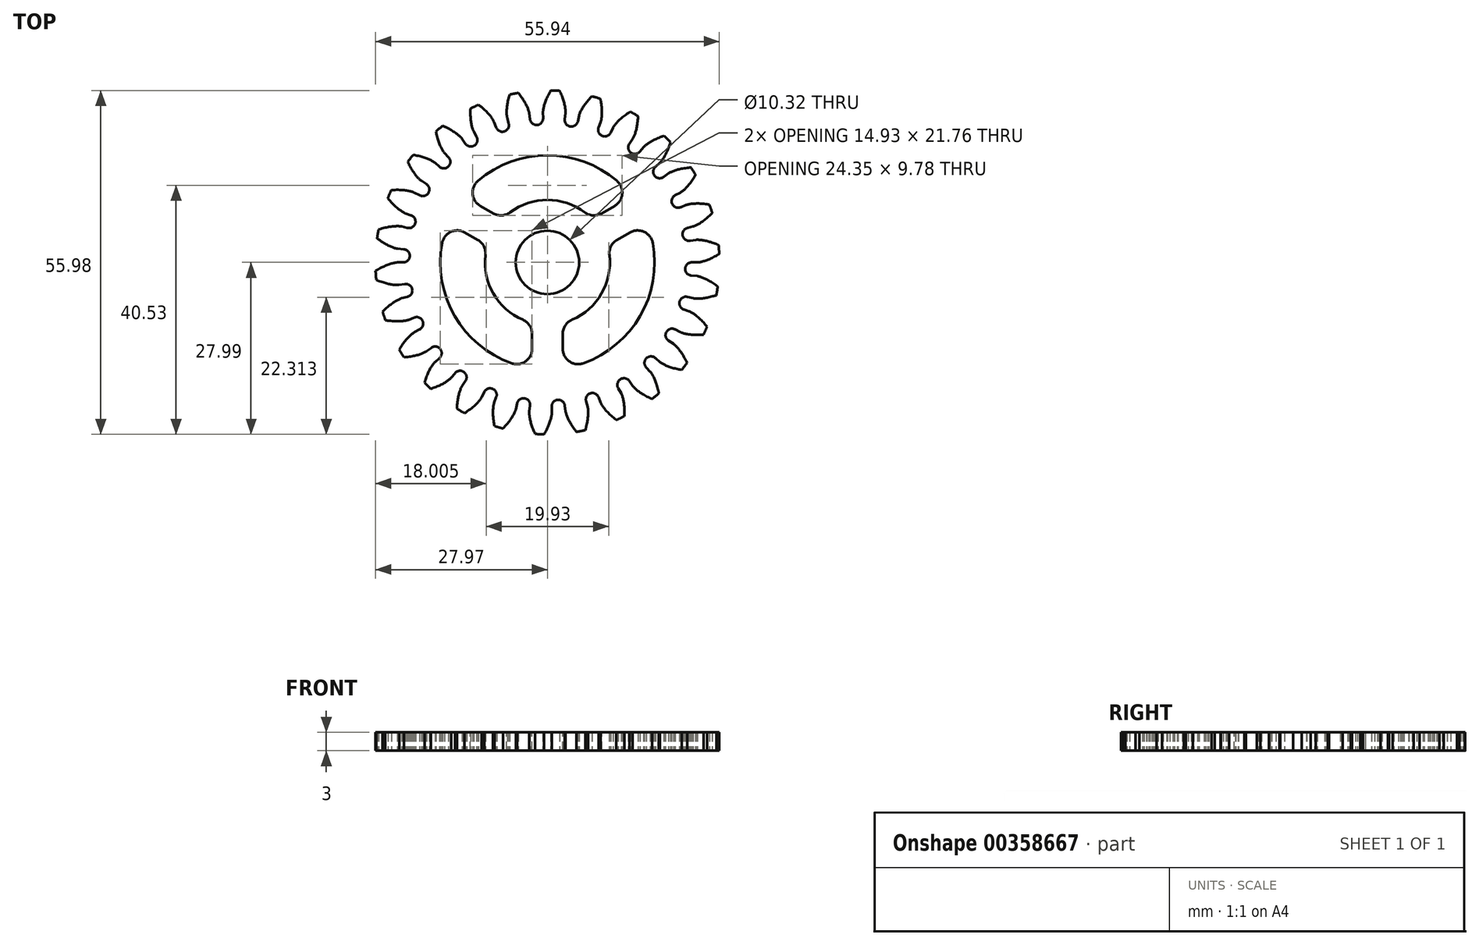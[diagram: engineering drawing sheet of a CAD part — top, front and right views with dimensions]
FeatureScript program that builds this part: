
annotation { "Feature Type Name" : "Feature", "Feature Type Description" : "" }
export const myFeature = defineFeature(function(context is Context, id is Id, definition is map)
    precondition{}
    {
        {
            assignVariable(context, id + "F0", {"name" : "T", "anyValue" : 26});
        }
        {
            assignVariable(context, id + "F1", {"name" : "SP", "anyValue" : 3});
        }
        {
            assignVariable(context, id + "F2", {"name" : "SF", "anyValue" : 2.5});
        }
        {
            var Q0;
            Q0=qCreatedBy(makeId("Top.planeOp"),FACE);
            var sketch = newSketch(context, id + "F3", { "sketchPlane" : qUnion([Q0])});
            skCircle(sketch, "E0", {"center": v(0, 0) * mm, "radius": 28 * mm});
            skCircle(sketch, "E1", {"center": v(0, 0) * mm, "radius": 26 * mm, "construction": true});
            skCircle(sketch, "E2", {"center": v(0, 0) * mm, "radius": 24.43 * mm, "construction": true});
            skCircle(sketch, "E3", {"center": v(0, 0) * mm, "radius": 23.5 * mm});
            skLineSegment(sketch, "E4", {"start": v(0, 0) * mm, "end": v(24.43, 0) * mm});
            skFitSpline(sketch, "E5", {"points": [v(24.43, 0) * mm, v(24.47, 0) * mm, v(24.6, 0.01) * mm, v(24.8, 0.04) * mm, v(25.1, 0.1) * mm, v(25.46, 0.2) * mm, v(25.9, 0.35) * mm, v(26.41, 0.56) * mm, v(26.99, 0.83) * mm, v(27.62, 1.17) * mm, v(28.3, 1.6) * mm], "startDerivative": vector(3.78, 0.15) * mm, "endDerivative": vector(13.99, 8.75) * mm});
            skLineSegment(sketch, "E6", {"start": v(0, 0) * mm, "end": v(27.97, -1.27) * mm, "construction": true});
            skLineSegment(sketch, "E7", {"start": v(0, 0) * mm, "end": v(26, 0.39) * mm, "construction": true});
            skFitSpline(sketch, "E8.MirrorCS", {"points": [v(24.33, -2.22) * mm, v(24.37, -2.23) * mm, v(24.5, -2.25) * mm, v(24.7, -2.3) * mm, v(24.98, -2.39) * mm, v(25.34, -2.52) * mm, v(25.77, -2.7) * mm, v(26.25, -2.96) * mm, v(26.8, -3.28) * mm, v(27.4, -3.68) * mm, v(28.03, -4.16) * mm], "startDerivative": vector(3.75, -0.5) * mm, "endDerivative": vector(13.13, -9.98) * mm});
            skLineSegment(sketch, "E9", {"start": v(0, 0) * mm, "end": v(24.33, -2.22) * mm});
            skSolve(sketch);
        }
        {
            var Q0;
            Q0=qCreatedBy(makeId("Top.planeOp"),FACE);
            var sketch = newSketch(context, id + "F4", { "sketchPlane" : qUnion([Q0])});
            skCircle(sketch, "E10", {"center": v(0, 0) * mm, "radius": 28 * mm});
            skSolve(sketch);
        }
        {
            var Q0;
            {var subQ0=sQuery(id+"F3.wireOp",EDGE,"E5");var subQ7=sQuery(id+"F3.wireOp",EDGE,"E0");var subQ8=makeQuery(id+"F3.imprint","INTERSECT",VERTEX,{"derivedFrom":[subQ7,subQ0]});Q0=makeQuery(id+"F3.imprint","IMPRINT",FACE,{"disambiguationData":[TD([[makeQuery(id+"F3.imprint","IMPRINT",EDGE,{"disambiguationData":[TD([[subQ8,1.0]])],"derivedFrom":subQ7}),1.0]])]});}
            extrude(context, id + "F5", {"entities" : qUnion([Q0]), "depth" : 6 * mm});
        }
        {
            var Q0;
            Q0=makeQuery(id+"F5.opExtrude","CAP_FACE",FACE,{"disambiguationData":[OSD([sQuery(id+"F3.wireOp",EDGE,"E0"),sQuery(id+"F3.wireOp",EDGE,"E3"),sQuery(id+"F3.wireOp",EDGE,"E4"),sQuery(id+"F3.wireOp",EDGE,"E5"),sQuery(id+"F3.wireOp",EDGE,"E8.MirrorCS"),sQuery(id+"F3.wireOp",EDGE,"E9")])],"isStart":true});
            var sketch = newSketch(context, id + "F6", { "sketchPlane" : qUnion([Q0])});
            skCircle(sketch, "E11", {"center": v(23.48, 1.07) * mm, "radius": 1.07 * mm});
            skSolve(sketch);
        }
        {
            var Q0;
            {var subQ1=makeQuery(id+"F5.opExtrude","CAP_EDGE",EDGE,{"disambiguationData":[OSD([sQuery(id+"F3.wireOp",EDGE,"E3")])],"isStart":true});Q0=makeQuery(id+"F6.imprint","IMPRINT",FACE,{"disambiguationData":[TD([[makeQuery(id+"F6.imprint","IMPRINT",EDGE,{"derivedFrom":subQ1}),-1.0]])]});}
            extrude(context, id + "F7", {"entities" : qUnion([Q0]), "operationType" : NewBodyOperationType.ADD, "oppositeDirection" : true, "depth" : 6 * mm});
        }
        {
            var Q0;
            Q0=makeQuery(id+"F4.imprint","IMPRINT",FACE,{"disambiguationData":[TD([[makeQuery(id+"F4.imprint","IMPRINT",EDGE,{"derivedFrom":sQuery(id+"F4.wireOp",EDGE,"E10")}),1.0]])]});
            extrude(context, id + "F8", {"entities" : qUnion([Q0]), "depth" : 3 * mm, "offsetDistance" : 25 * mm});
        }
        {
            var Q0;
            Q0=makeQuery(id+"F5.opExtrude","SWEPT_BODY",BODY,{"disambiguationData":[OSD([sQuery(id+"F3.wireOp",EDGE,"E0"),sQuery(id+"F3.wireOp",EDGE,"E3"),sQuery(id+"F3.wireOp",EDGE,"E4"),sQuery(id+"F3.wireOp",EDGE,"E5"),sQuery(id+"F3.wireOp",EDGE,"E8.MirrorCS"),sQuery(id+"F3.wireOp",EDGE,"E9")])]});
            var Q1;
            Q1=makeQuery(id+"F8.opExtrude","CAP_EDGE",EDGE,{"disambiguationData":[OSD([sQuery(id+"F4.wireOp",EDGE,"E10")])],"isStart":false});
            circularPattern(context, id + "F9", {"entities" : qUnion([Q0]), "axis" : qUnion([Q1]), "angle" : 360 * degree, "instanceCount" : getVariable(context, 'T'), "equalSpace" : true});
        }
        {
            var Q0;
            Q0=makeQuery(id+"F9.opPattern","COPY",BODY,{"derivedFrom":makeQuery(id+"F5.opExtrude","SWEPT_BODY",BODY,{"disambiguationData":[OSD([sQuery(id+"F3.wireOp",EDGE,"E0"),sQuery(id+"F3.wireOp",EDGE,"E3"),sQuery(id+"F3.wireOp",EDGE,"E4"),sQuery(id+"F3.wireOp",EDGE,"E5"),sQuery(id+"F3.wireOp",EDGE,"E8.MirrorCS"),sQuery(id+"F3.wireOp",EDGE,"E9")])]}),"instanceName":"5"});
            var Q1;
            Q1=makeQuery(id+"F9.opPattern","COPY",BODY,{"derivedFrom":makeQuery(id+"F5.opExtrude","SWEPT_BODY",BODY,{"disambiguationData":[OSD([sQuery(id+"F3.wireOp",EDGE,"E0"),sQuery(id+"F3.wireOp",EDGE,"E3"),sQuery(id+"F3.wireOp",EDGE,"E4"),sQuery(id+"F3.wireOp",EDGE,"E5"),sQuery(id+"F3.wireOp",EDGE,"E8.MirrorCS"),sQuery(id+"F3.wireOp",EDGE,"E9")])]}),"instanceName":"6"});
            var Q2;
            Q2=makeQuery(id+"F9.opPattern","COPY",BODY,{"derivedFrom":makeQuery(id+"F5.opExtrude","SWEPT_BODY",BODY,{"disambiguationData":[OSD([sQuery(id+"F3.wireOp",EDGE,"E0"),sQuery(id+"F3.wireOp",EDGE,"E3"),sQuery(id+"F3.wireOp",EDGE,"E4"),sQuery(id+"F3.wireOp",EDGE,"E5"),sQuery(id+"F3.wireOp",EDGE,"E8.MirrorCS"),sQuery(id+"F3.wireOp",EDGE,"E9")])]}),"instanceName":"7"});
            var Q3;
            Q3=makeQuery(id+"F9.opPattern","COPY",BODY,{"derivedFrom":makeQuery(id+"F5.opExtrude","SWEPT_BODY",BODY,{"disambiguationData":[OSD([sQuery(id+"F3.wireOp",EDGE,"E0"),sQuery(id+"F3.wireOp",EDGE,"E3"),sQuery(id+"F3.wireOp",EDGE,"E4"),sQuery(id+"F3.wireOp",EDGE,"E5"),sQuery(id+"F3.wireOp",EDGE,"E8.MirrorCS"),sQuery(id+"F3.wireOp",EDGE,"E9")])]}),"instanceName":"8"});
            var Q4;
            Q4=makeQuery(id+"F9.opPattern","COPY",BODY,{"derivedFrom":makeQuery(id+"F5.opExtrude","SWEPT_BODY",BODY,{"disambiguationData":[OSD([sQuery(id+"F3.wireOp",EDGE,"E0"),sQuery(id+"F3.wireOp",EDGE,"E3"),sQuery(id+"F3.wireOp",EDGE,"E4"),sQuery(id+"F3.wireOp",EDGE,"E5"),sQuery(id+"F3.wireOp",EDGE,"E8.MirrorCS"),sQuery(id+"F3.wireOp",EDGE,"E9")])]}),"instanceName":"9"});
            var Q5;
            Q5=makeQuery(id+"F9.opPattern","COPY",BODY,{"derivedFrom":makeQuery(id+"F5.opExtrude","SWEPT_BODY",BODY,{"disambiguationData":[OSD([sQuery(id+"F3.wireOp",EDGE,"E0"),sQuery(id+"F3.wireOp",EDGE,"E3"),sQuery(id+"F3.wireOp",EDGE,"E4"),sQuery(id+"F3.wireOp",EDGE,"E5"),sQuery(id+"F3.wireOp",EDGE,"E8.MirrorCS"),sQuery(id+"F3.wireOp",EDGE,"E9")])]}),"instanceName":"10"});
            var Q6;
            Q6=makeQuery(id+"F9.opPattern","COPY",BODY,{"derivedFrom":makeQuery(id+"F5.opExtrude","SWEPT_BODY",BODY,{"disambiguationData":[OSD([sQuery(id+"F3.wireOp",EDGE,"E0"),sQuery(id+"F3.wireOp",EDGE,"E3"),sQuery(id+"F3.wireOp",EDGE,"E4"),sQuery(id+"F3.wireOp",EDGE,"E5"),sQuery(id+"F3.wireOp",EDGE,"E8.MirrorCS"),sQuery(id+"F3.wireOp",EDGE,"E9")])]}),"instanceName":"11"});
            var Q7;
            Q7=makeQuery(id+"F9.opPattern","COPY",BODY,{"derivedFrom":makeQuery(id+"F5.opExtrude","SWEPT_BODY",BODY,{"disambiguationData":[OSD([sQuery(id+"F3.wireOp",EDGE,"E0"),sQuery(id+"F3.wireOp",EDGE,"E3"),sQuery(id+"F3.wireOp",EDGE,"E4"),sQuery(id+"F3.wireOp",EDGE,"E5"),sQuery(id+"F3.wireOp",EDGE,"E8.MirrorCS"),sQuery(id+"F3.wireOp",EDGE,"E9")])]}),"instanceName":"12"});
            var Q8;
            Q8=makeQuery(id+"F9.opPattern","COPY",BODY,{"derivedFrom":makeQuery(id+"F5.opExtrude","SWEPT_BODY",BODY,{"disambiguationData":[OSD([sQuery(id+"F3.wireOp",EDGE,"E0"),sQuery(id+"F3.wireOp",EDGE,"E3"),sQuery(id+"F3.wireOp",EDGE,"E4"),sQuery(id+"F3.wireOp",EDGE,"E5"),sQuery(id+"F3.wireOp",EDGE,"E8.MirrorCS"),sQuery(id+"F3.wireOp",EDGE,"E9")])]}),"instanceName":"13"});
            var Q9;
            Q9=makeQuery(id+"F9.opPattern","COPY",BODY,{"derivedFrom":makeQuery(id+"F5.opExtrude","SWEPT_BODY",BODY,{"disambiguationData":[OSD([sQuery(id+"F3.wireOp",EDGE,"E0"),sQuery(id+"F3.wireOp",EDGE,"E3"),sQuery(id+"F3.wireOp",EDGE,"E4"),sQuery(id+"F3.wireOp",EDGE,"E5"),sQuery(id+"F3.wireOp",EDGE,"E8.MirrorCS"),sQuery(id+"F3.wireOp",EDGE,"E9")])]}),"instanceName":"14"});
            var Q10;
            Q10=makeQuery(id+"F9.opPattern","COPY",BODY,{"derivedFrom":makeQuery(id+"F5.opExtrude","SWEPT_BODY",BODY,{"disambiguationData":[OSD([sQuery(id+"F3.wireOp",EDGE,"E0"),sQuery(id+"F3.wireOp",EDGE,"E3"),sQuery(id+"F3.wireOp",EDGE,"E4"),sQuery(id+"F3.wireOp",EDGE,"E5"),sQuery(id+"F3.wireOp",EDGE,"E8.MirrorCS"),sQuery(id+"F3.wireOp",EDGE,"E9")])]}),"instanceName":"15"});
            var Q11;
            Q11=makeQuery(id+"F9.opPattern","COPY",BODY,{"derivedFrom":makeQuery(id+"F5.opExtrude","SWEPT_BODY",BODY,{"disambiguationData":[OSD([sQuery(id+"F3.wireOp",EDGE,"E0"),sQuery(id+"F3.wireOp",EDGE,"E3"),sQuery(id+"F3.wireOp",EDGE,"E4"),sQuery(id+"F3.wireOp",EDGE,"E5"),sQuery(id+"F3.wireOp",EDGE,"E8.MirrorCS"),sQuery(id+"F3.wireOp",EDGE,"E9")])]}),"instanceName":"16"});
            var Q12;
            Q12=makeQuery(id+"F9.opPattern","COPY",BODY,{"derivedFrom":makeQuery(id+"F5.opExtrude","SWEPT_BODY",BODY,{"disambiguationData":[OSD([sQuery(id+"F3.wireOp",EDGE,"E0"),sQuery(id+"F3.wireOp",EDGE,"E3"),sQuery(id+"F3.wireOp",EDGE,"E4"),sQuery(id+"F3.wireOp",EDGE,"E5"),sQuery(id+"F3.wireOp",EDGE,"E8.MirrorCS"),sQuery(id+"F3.wireOp",EDGE,"E9")])]}),"instanceName":"17"});
            var Q13;
            Q13=makeQuery(id+"F9.opPattern","COPY",BODY,{"derivedFrom":makeQuery(id+"F5.opExtrude","SWEPT_BODY",BODY,{"disambiguationData":[OSD([sQuery(id+"F3.wireOp",EDGE,"E0"),sQuery(id+"F3.wireOp",EDGE,"E3"),sQuery(id+"F3.wireOp",EDGE,"E4"),sQuery(id+"F3.wireOp",EDGE,"E5"),sQuery(id+"F3.wireOp",EDGE,"E8.MirrorCS"),sQuery(id+"F3.wireOp",EDGE,"E9")])]}),"instanceName":"18"});
            var Q14;
            Q14=makeQuery(id+"F9.opPattern","COPY",BODY,{"derivedFrom":makeQuery(id+"F5.opExtrude","SWEPT_BODY",BODY,{"disambiguationData":[OSD([sQuery(id+"F3.wireOp",EDGE,"E0"),sQuery(id+"F3.wireOp",EDGE,"E3"),sQuery(id+"F3.wireOp",EDGE,"E4"),sQuery(id+"F3.wireOp",EDGE,"E5"),sQuery(id+"F3.wireOp",EDGE,"E8.MirrorCS"),sQuery(id+"F3.wireOp",EDGE,"E9")])]}),"instanceName":"19"});
            var Q15;
            Q15=makeQuery(id+"F9.opPattern","COPY",BODY,{"derivedFrom":makeQuery(id+"F5.opExtrude","SWEPT_BODY",BODY,{"disambiguationData":[OSD([sQuery(id+"F3.wireOp",EDGE,"E0"),sQuery(id+"F3.wireOp",EDGE,"E3"),sQuery(id+"F3.wireOp",EDGE,"E4"),sQuery(id+"F3.wireOp",EDGE,"E5"),sQuery(id+"F3.wireOp",EDGE,"E8.MirrorCS"),sQuery(id+"F3.wireOp",EDGE,"E9")])]}),"instanceName":"20"});
            var Q16;
            Q16=makeQuery(id+"F9.opPattern","COPY",BODY,{"derivedFrom":makeQuery(id+"F5.opExtrude","SWEPT_BODY",BODY,{"disambiguationData":[OSD([sQuery(id+"F3.wireOp",EDGE,"E0"),sQuery(id+"F3.wireOp",EDGE,"E3"),sQuery(id+"F3.wireOp",EDGE,"E4"),sQuery(id+"F3.wireOp",EDGE,"E5"),sQuery(id+"F3.wireOp",EDGE,"E8.MirrorCS"),sQuery(id+"F3.wireOp",EDGE,"E9")])]}),"instanceName":"21"});
            var Q17;
            Q17=makeQuery(id+"F9.opPattern","COPY",BODY,{"derivedFrom":makeQuery(id+"F5.opExtrude","SWEPT_BODY",BODY,{"disambiguationData":[OSD([sQuery(id+"F3.wireOp",EDGE,"E0"),sQuery(id+"F3.wireOp",EDGE,"E3"),sQuery(id+"F3.wireOp",EDGE,"E4"),sQuery(id+"F3.wireOp",EDGE,"E5"),sQuery(id+"F3.wireOp",EDGE,"E8.MirrorCS"),sQuery(id+"F3.wireOp",EDGE,"E9")])]}),"instanceName":"22"});
            var Q18;
            Q18=makeQuery(id+"F9.opPattern","COPY",BODY,{"derivedFrom":makeQuery(id+"F5.opExtrude","SWEPT_BODY",BODY,{"disambiguationData":[OSD([sQuery(id+"F3.wireOp",EDGE,"E0"),sQuery(id+"F3.wireOp",EDGE,"E3"),sQuery(id+"F3.wireOp",EDGE,"E4"),sQuery(id+"F3.wireOp",EDGE,"E5"),sQuery(id+"F3.wireOp",EDGE,"E8.MirrorCS"),sQuery(id+"F3.wireOp",EDGE,"E9")])]}),"instanceName":"23"});
            var Q19;
            Q19=makeQuery(id+"F9.opPattern","COPY",BODY,{"derivedFrom":makeQuery(id+"F5.opExtrude","SWEPT_BODY",BODY,{"disambiguationData":[OSD([sQuery(id+"F3.wireOp",EDGE,"E0"),sQuery(id+"F3.wireOp",EDGE,"E3"),sQuery(id+"F3.wireOp",EDGE,"E4"),sQuery(id+"F3.wireOp",EDGE,"E5"),sQuery(id+"F3.wireOp",EDGE,"E8.MirrorCS"),sQuery(id+"F3.wireOp",EDGE,"E9")])]}),"instanceName":"24"});
            var Q20;
            Q20=makeQuery(id+"F9.opPattern","COPY",BODY,{"derivedFrom":makeQuery(id+"F5.opExtrude","SWEPT_BODY",BODY,{"disambiguationData":[OSD([sQuery(id+"F3.wireOp",EDGE,"E0"),sQuery(id+"F3.wireOp",EDGE,"E3"),sQuery(id+"F3.wireOp",EDGE,"E4"),sQuery(id+"F3.wireOp",EDGE,"E5"),sQuery(id+"F3.wireOp",EDGE,"E8.MirrorCS"),sQuery(id+"F3.wireOp",EDGE,"E9")])]}),"instanceName":"25"});
            var Q21;
            Q21=makeQuery(id+"F9.opPattern","COPY",BODY,{"derivedFrom":makeQuery(id+"F5.opExtrude","SWEPT_BODY",BODY,{"disambiguationData":[OSD([sQuery(id+"F3.wireOp",EDGE,"E0"),sQuery(id+"F3.wireOp",EDGE,"E3"),sQuery(id+"F3.wireOp",EDGE,"E4"),sQuery(id+"F3.wireOp",EDGE,"E5"),sQuery(id+"F3.wireOp",EDGE,"E8.MirrorCS"),sQuery(id+"F3.wireOp",EDGE,"E9")])]}),"instanceName":"26"});
            var Q22;
            Q22=makeQuery(id+"F9.opPattern","COPY",BODY,{"derivedFrom":makeQuery(id+"F5.opExtrude","SWEPT_BODY",BODY,{"disambiguationData":[OSD([sQuery(id+"F3.wireOp",EDGE,"E0"),sQuery(id+"F3.wireOp",EDGE,"E3"),sQuery(id+"F3.wireOp",EDGE,"E4"),sQuery(id+"F3.wireOp",EDGE,"E5"),sQuery(id+"F3.wireOp",EDGE,"E8.MirrorCS"),sQuery(id+"F3.wireOp",EDGE,"E9")])]}),"instanceName":"27"});
            var Q23;
            Q23=makeQuery(id+"F9.opPattern","COPY",BODY,{"derivedFrom":makeQuery(id+"F5.opExtrude","SWEPT_BODY",BODY,{"disambiguationData":[OSD([sQuery(id+"F3.wireOp",EDGE,"E0"),sQuery(id+"F3.wireOp",EDGE,"E3"),sQuery(id+"F3.wireOp",EDGE,"E4"),sQuery(id+"F3.wireOp",EDGE,"E5"),sQuery(id+"F3.wireOp",EDGE,"E8.MirrorCS"),sQuery(id+"F3.wireOp",EDGE,"E9")])]}),"instanceName":"28"});
            var Q24;
            Q24=makeQuery(id+"F9.opPattern","COPY",BODY,{"derivedFrom":makeQuery(id+"F5.opExtrude","SWEPT_BODY",BODY,{"disambiguationData":[OSD([sQuery(id+"F3.wireOp",EDGE,"E0"),sQuery(id+"F3.wireOp",EDGE,"E3"),sQuery(id+"F3.wireOp",EDGE,"E4"),sQuery(id+"F3.wireOp",EDGE,"E5"),sQuery(id+"F3.wireOp",EDGE,"E8.MirrorCS"),sQuery(id+"F3.wireOp",EDGE,"E9")])]}),"instanceName":"29"});
            var Q25;
            Q25=makeQuery(id+"F5.opExtrude","SWEPT_BODY",BODY,{"disambiguationData":[OSD([sQuery(id+"F3.wireOp",EDGE,"E0"),sQuery(id+"F3.wireOp",EDGE,"E3"),sQuery(id+"F3.wireOp",EDGE,"E4"),sQuery(id+"F3.wireOp",EDGE,"E5"),sQuery(id+"F3.wireOp",EDGE,"E8.MirrorCS"),sQuery(id+"F3.wireOp",EDGE,"E9")])]});
            var Q26;
            Q26=makeQuery(id+"F9.opPattern","COPY",BODY,{"derivedFrom":makeQuery(id+"F5.opExtrude","SWEPT_BODY",BODY,{"disambiguationData":[OSD([sQuery(id+"F3.wireOp",EDGE,"E0"),sQuery(id+"F3.wireOp",EDGE,"E3"),sQuery(id+"F3.wireOp",EDGE,"E4"),sQuery(id+"F3.wireOp",EDGE,"E5"),sQuery(id+"F3.wireOp",EDGE,"E8.MirrorCS"),sQuery(id+"F3.wireOp",EDGE,"E9")])]}),"instanceName":"1"});
            var Q27;
            Q27=makeQuery(id+"F9.opPattern","COPY",BODY,{"derivedFrom":makeQuery(id+"F5.opExtrude","SWEPT_BODY",BODY,{"disambiguationData":[OSD([sQuery(id+"F3.wireOp",EDGE,"E0"),sQuery(id+"F3.wireOp",EDGE,"E3"),sQuery(id+"F3.wireOp",EDGE,"E4"),sQuery(id+"F3.wireOp",EDGE,"E5"),sQuery(id+"F3.wireOp",EDGE,"E8.MirrorCS"),sQuery(id+"F3.wireOp",EDGE,"E9")])]}),"instanceName":"2"});
            var Q28;
            Q28=makeQuery(id+"F9.opPattern","COPY",BODY,{"derivedFrom":makeQuery(id+"F5.opExtrude","SWEPT_BODY",BODY,{"disambiguationData":[OSD([sQuery(id+"F3.wireOp",EDGE,"E0"),sQuery(id+"F3.wireOp",EDGE,"E3"),sQuery(id+"F3.wireOp",EDGE,"E4"),sQuery(id+"F3.wireOp",EDGE,"E5"),sQuery(id+"F3.wireOp",EDGE,"E8.MirrorCS"),sQuery(id+"F3.wireOp",EDGE,"E9")])]}),"instanceName":"3"});
            var Q29;
            Q29=makeQuery(id+"F9.opPattern","COPY",BODY,{"derivedFrom":makeQuery(id+"F5.opExtrude","SWEPT_BODY",BODY,{"disambiguationData":[OSD([sQuery(id+"F3.wireOp",EDGE,"E0"),sQuery(id+"F3.wireOp",EDGE,"E3"),sQuery(id+"F3.wireOp",EDGE,"E4"),sQuery(id+"F3.wireOp",EDGE,"E5"),sQuery(id+"F3.wireOp",EDGE,"E8.MirrorCS"),sQuery(id+"F3.wireOp",EDGE,"E9")])]}),"instanceName":"4"});
            var Q30;
            Q30=makeQuery(id+"F9.opPattern","COPY",BODY,{"derivedFrom":makeQuery(id+"F5.opExtrude","SWEPT_BODY",BODY,{"disambiguationData":[OSD([sQuery(id+"F3.wireOp",EDGE,"E0"),sQuery(id+"F3.wireOp",EDGE,"E3"),sQuery(id+"F3.wireOp",EDGE,"E5"),sQuery(id+"F3.wireOp",EDGE,"E8.MirrorCS")])]}),"instanceName":"30"});
            var Q31;
            Q31=makeQuery(id+"F9.opPattern","COPY",BODY,{"derivedFrom":makeQuery(id+"F5.opExtrude","SWEPT_BODY",BODY,{"disambiguationData":[OSD([sQuery(id+"F3.wireOp",EDGE,"E0"),sQuery(id+"F3.wireOp",EDGE,"E3"),sQuery(id+"F3.wireOp",EDGE,"E5"),sQuery(id+"F3.wireOp",EDGE,"E8.MirrorCS")])]}),"instanceName":"31"});
            var Q32;
            Q32=makeQuery(id+"F9.opPattern","COPY",BODY,{"derivedFrom":makeQuery(id+"F5.opExtrude","SWEPT_BODY",BODY,{"disambiguationData":[OSD([sQuery(id+"F3.wireOp",EDGE,"E0"),sQuery(id+"F3.wireOp",EDGE,"E3"),sQuery(id+"F3.wireOp",EDGE,"E5"),sQuery(id+"F3.wireOp",EDGE,"E8.MirrorCS")])]}),"instanceName":"32"});
            var Q33;
            Q33=makeQuery(id+"F9.opPattern","COPY",BODY,{"derivedFrom":makeQuery(id+"F5.opExtrude","SWEPT_BODY",BODY,{"disambiguationData":[OSD([sQuery(id+"F3.wireOp",EDGE,"E0"),sQuery(id+"F3.wireOp",EDGE,"E3"),sQuery(id+"F3.wireOp",EDGE,"E5"),sQuery(id+"F3.wireOp",EDGE,"E8.MirrorCS")])]}),"instanceName":"33"});
            var Q34;
            Q34=makeQuery(id+"F9.opPattern","COPY",BODY,{"derivedFrom":makeQuery(id+"F5.opExtrude","SWEPT_BODY",BODY,{"disambiguationData":[OSD([sQuery(id+"F3.wireOp",EDGE,"E0"),sQuery(id+"F3.wireOp",EDGE,"E3"),sQuery(id+"F3.wireOp",EDGE,"E5"),sQuery(id+"F3.wireOp",EDGE,"E8.MirrorCS")])]}),"instanceName":"34"});
            var Q35;
            Q35=makeQuery(id+"F9.opPattern","COPY",BODY,{"derivedFrom":makeQuery(id+"F5.opExtrude","SWEPT_BODY",BODY,{"disambiguationData":[OSD([sQuery(id+"F3.wireOp",EDGE,"E0"),sQuery(id+"F3.wireOp",EDGE,"E3"),sQuery(id+"F3.wireOp",EDGE,"E5"),sQuery(id+"F3.wireOp",EDGE,"E8.MirrorCS")])]}),"instanceName":"35"});
            var Q36;
            Q36=makeQuery(id+"F9.opPattern","COPY",BODY,{"derivedFrom":makeQuery(id+"F5.opExtrude","SWEPT_BODY",BODY,{"disambiguationData":[OSD([sQuery(id+"F3.wireOp",EDGE,"E0"),sQuery(id+"F3.wireOp",EDGE,"E3"),sQuery(id+"F3.wireOp",EDGE,"E5"),sQuery(id+"F3.wireOp",EDGE,"E8.MirrorCS")])]}),"instanceName":"36"});
            var Q37;
            Q37=makeQuery(id+"F9.opPattern","COPY",BODY,{"derivedFrom":makeQuery(id+"F5.opExtrude","SWEPT_BODY",BODY,{"disambiguationData":[OSD([sQuery(id+"F3.wireOp",EDGE,"E0"),sQuery(id+"F3.wireOp",EDGE,"E3"),sQuery(id+"F3.wireOp",EDGE,"E5"),sQuery(id+"F3.wireOp",EDGE,"E8.MirrorCS")])]}),"instanceName":"37"});
            var Q38;
            Q38=makeQuery(id+"F9.opPattern","COPY",BODY,{"derivedFrom":makeQuery(id+"F5.opExtrude","SWEPT_BODY",BODY,{"disambiguationData":[OSD([sQuery(id+"F3.wireOp",EDGE,"E0"),sQuery(id+"F3.wireOp",EDGE,"E3"),sQuery(id+"F3.wireOp",EDGE,"E5"),sQuery(id+"F3.wireOp",EDGE,"E8.MirrorCS")])]}),"instanceName":"38"});
            var Q39;
            Q39=makeQuery(id+"F9.opPattern","COPY",BODY,{"derivedFrom":makeQuery(id+"F5.opExtrude","SWEPT_BODY",BODY,{"disambiguationData":[OSD([sQuery(id+"F3.wireOp",EDGE,"E0"),sQuery(id+"F3.wireOp",EDGE,"E3"),sQuery(id+"F3.wireOp",EDGE,"E5"),sQuery(id+"F3.wireOp",EDGE,"E8.MirrorCS")])]}),"instanceName":"39"});
            var Q40;
            Q40=makeQuery(id+"F9.opPattern","COPY",BODY,{"derivedFrom":makeQuery(id+"F5.opExtrude","SWEPT_BODY",BODY,{"disambiguationData":[OSD([sQuery(id+"F3.wireOp",EDGE,"E0"),sQuery(id+"F3.wireOp",EDGE,"E3"),sQuery(id+"F3.wireOp",EDGE,"E5"),sQuery(id+"F3.wireOp",EDGE,"E8.MirrorCS")])]}),"instanceName":"40"});
            var Q41;
            Q41=makeQuery(id+"F9.opPattern","COPY",BODY,{"derivedFrom":makeQuery(id+"F5.opExtrude","SWEPT_BODY",BODY,{"disambiguationData":[OSD([sQuery(id+"F3.wireOp",EDGE,"E0"),sQuery(id+"F3.wireOp",EDGE,"E3"),sQuery(id+"F3.wireOp",EDGE,"E5"),sQuery(id+"F3.wireOp",EDGE,"E8.MirrorCS")])]}),"instanceName":"41"});
            var Q42;
            Q42=makeQuery(id+"F9.opPattern","COPY",BODY,{"derivedFrom":makeQuery(id+"F5.opExtrude","SWEPT_BODY",BODY,{"disambiguationData":[OSD([sQuery(id+"F3.wireOp",EDGE,"E0"),sQuery(id+"F3.wireOp",EDGE,"E3"),sQuery(id+"F3.wireOp",EDGE,"E5"),sQuery(id+"F3.wireOp",EDGE,"E8.MirrorCS")])]}),"instanceName":"42"});
            var Q43;
            Q43=makeQuery(id+"F9.opPattern","COPY",BODY,{"derivedFrom":makeQuery(id+"F5.opExtrude","SWEPT_BODY",BODY,{"disambiguationData":[OSD([sQuery(id+"F3.wireOp",EDGE,"E0"),sQuery(id+"F3.wireOp",EDGE,"E3"),sQuery(id+"F3.wireOp",EDGE,"E5"),sQuery(id+"F3.wireOp",EDGE,"E8.MirrorCS")])]}),"instanceName":"43"});
            var Q44;
            Q44=makeQuery(id+"F9.opPattern","COPY",BODY,{"derivedFrom":makeQuery(id+"F5.opExtrude","SWEPT_BODY",BODY,{"disambiguationData":[OSD([sQuery(id+"F3.wireOp",EDGE,"E0"),sQuery(id+"F3.wireOp",EDGE,"E3"),sQuery(id+"F3.wireOp",EDGE,"E5"),sQuery(id+"F3.wireOp",EDGE,"E8.MirrorCS")])]}),"instanceName":"44"});
            var Q45;
            Q45=makeQuery(id+"F9.opPattern","COPY",BODY,{"derivedFrom":makeQuery(id+"F5.opExtrude","SWEPT_BODY",BODY,{"disambiguationData":[OSD([sQuery(id+"F3.wireOp",EDGE,"E0"),sQuery(id+"F3.wireOp",EDGE,"E3"),sQuery(id+"F3.wireOp",EDGE,"E5"),sQuery(id+"F3.wireOp",EDGE,"E8.MirrorCS")])]}),"instanceName":"45"});
            var Q46;
            Q46=makeQuery(id+"F9.opPattern","COPY",BODY,{"derivedFrom":makeQuery(id+"F5.opExtrude","SWEPT_BODY",BODY,{"disambiguationData":[OSD([sQuery(id+"F3.wireOp",EDGE,"E0"),sQuery(id+"F3.wireOp",EDGE,"E3"),sQuery(id+"F3.wireOp",EDGE,"E5"),sQuery(id+"F3.wireOp",EDGE,"E8.MirrorCS")])]}),"instanceName":"46"});
            var Q47;
            Q47=makeQuery(id+"F9.opPattern","COPY",BODY,{"derivedFrom":makeQuery(id+"F5.opExtrude","SWEPT_BODY",BODY,{"disambiguationData":[OSD([sQuery(id+"F3.wireOp",EDGE,"E0"),sQuery(id+"F3.wireOp",EDGE,"E3"),sQuery(id+"F3.wireOp",EDGE,"E5"),sQuery(id+"F3.wireOp",EDGE,"E8.MirrorCS")])]}),"instanceName":"47"});
            var Q48;
            Q48=makeQuery(id+"F9.opPattern","COPY",BODY,{"derivedFrom":makeQuery(id+"F5.opExtrude","SWEPT_BODY",BODY,{"disambiguationData":[OSD([sQuery(id+"F3.wireOp",EDGE,"E0"),sQuery(id+"F3.wireOp",EDGE,"E3"),sQuery(id+"F3.wireOp",EDGE,"E5"),sQuery(id+"F3.wireOp",EDGE,"E8.MirrorCS")])]}),"instanceName":"48"});
            var Q49;
            Q49=makeQuery(id+"F9.opPattern","COPY",BODY,{"derivedFrom":makeQuery(id+"F5.opExtrude","SWEPT_BODY",BODY,{"disambiguationData":[OSD([sQuery(id+"F3.wireOp",EDGE,"E0"),sQuery(id+"F3.wireOp",EDGE,"E3"),sQuery(id+"F3.wireOp",EDGE,"E5"),sQuery(id+"F3.wireOp",EDGE,"E8.MirrorCS")])]}),"instanceName":"49"});
            var Q50;
            Q50=makeQuery(id+"F9.opPattern","COPY",BODY,{"derivedFrom":makeQuery(id+"F5.opExtrude","SWEPT_BODY",BODY,{"disambiguationData":[OSD([sQuery(id+"F3.wireOp",EDGE,"E0"),sQuery(id+"F3.wireOp",EDGE,"E3"),sQuery(id+"F3.wireOp",EDGE,"E5"),sQuery(id+"F3.wireOp",EDGE,"E8.MirrorCS")])]}),"instanceName":"50"});
            var Q51;
            Q51=makeQuery(id+"F9.opPattern","COPY",BODY,{"derivedFrom":makeQuery(id+"F5.opExtrude","SWEPT_BODY",BODY,{"disambiguationData":[OSD([sQuery(id+"F3.wireOp",EDGE,"E0"),sQuery(id+"F3.wireOp",EDGE,"E3"),sQuery(id+"F3.wireOp",EDGE,"E5"),sQuery(id+"F3.wireOp",EDGE,"E8.MirrorCS")])]}),"instanceName":"51"});
            var Q52;
            Q52=makeQuery(id+"F9.opPattern","COPY",BODY,{"derivedFrom":makeQuery(id+"F5.opExtrude","SWEPT_BODY",BODY,{"disambiguationData":[OSD([sQuery(id+"F3.wireOp",EDGE,"E0"),sQuery(id+"F3.wireOp",EDGE,"E3"),sQuery(id+"F3.wireOp",EDGE,"E5"),sQuery(id+"F3.wireOp",EDGE,"E8.MirrorCS")])]}),"instanceName":"52"});
            var Q53;
            Q53=makeQuery(id+"F9.opPattern","COPY",BODY,{"derivedFrom":makeQuery(id+"F5.opExtrude","SWEPT_BODY",BODY,{"disambiguationData":[OSD([sQuery(id+"F3.wireOp",EDGE,"E0"),sQuery(id+"F3.wireOp",EDGE,"E3"),sQuery(id+"F3.wireOp",EDGE,"E5"),sQuery(id+"F3.wireOp",EDGE,"E8.MirrorCS")])]}),"instanceName":"53"});
            var Q54;
            Q54=makeQuery(id+"F9.opPattern","COPY",BODY,{"derivedFrom":makeQuery(id+"F5.opExtrude","SWEPT_BODY",BODY,{"disambiguationData":[OSD([sQuery(id+"F3.wireOp",EDGE,"E0"),sQuery(id+"F3.wireOp",EDGE,"E3"),sQuery(id+"F3.wireOp",EDGE,"E5"),sQuery(id+"F3.wireOp",EDGE,"E8.MirrorCS")])]}),"instanceName":"54"});
            var Q55;
            Q55=makeQuery(id+"F9.opPattern","COPY",BODY,{"derivedFrom":makeQuery(id+"F5.opExtrude","SWEPT_BODY",BODY,{"disambiguationData":[OSD([sQuery(id+"F3.wireOp",EDGE,"E0"),sQuery(id+"F3.wireOp",EDGE,"E3"),sQuery(id+"F3.wireOp",EDGE,"E5"),sQuery(id+"F3.wireOp",EDGE,"E8.MirrorCS")])]}),"instanceName":"55"});
            var Q56;
            Q56=makeQuery(id+"F9.opPattern","COPY",BODY,{"derivedFrom":makeQuery(id+"F5.opExtrude","SWEPT_BODY",BODY,{"disambiguationData":[OSD([sQuery(id+"F3.wireOp",EDGE,"E0"),sQuery(id+"F3.wireOp",EDGE,"E3"),sQuery(id+"F3.wireOp",EDGE,"E5"),sQuery(id+"F3.wireOp",EDGE,"E8.MirrorCS")])]}),"instanceName":"56"});
            var Q57;
            Q57=makeQuery(id+"F9.opPattern","COPY",BODY,{"derivedFrom":makeQuery(id+"F5.opExtrude","SWEPT_BODY",BODY,{"disambiguationData":[OSD([sQuery(id+"F3.wireOp",EDGE,"E0"),sQuery(id+"F3.wireOp",EDGE,"E3"),sQuery(id+"F3.wireOp",EDGE,"E5"),sQuery(id+"F3.wireOp",EDGE,"E8.MirrorCS")])]}),"instanceName":"57"});
            var Q58;
            Q58=makeQuery(id+"F9.opPattern","COPY",BODY,{"derivedFrom":makeQuery(id+"F5.opExtrude","SWEPT_BODY",BODY,{"disambiguationData":[OSD([sQuery(id+"F3.wireOp",EDGE,"E0"),sQuery(id+"F3.wireOp",EDGE,"E3"),sQuery(id+"F3.wireOp",EDGE,"E5"),sQuery(id+"F3.wireOp",EDGE,"E8.MirrorCS")])]}),"instanceName":"58"});
            var Q59;
            Q59=makeQuery(id+"F9.opPattern","COPY",BODY,{"derivedFrom":makeQuery(id+"F5.opExtrude","SWEPT_BODY",BODY,{"disambiguationData":[OSD([sQuery(id+"F3.wireOp",EDGE,"E0"),sQuery(id+"F3.wireOp",EDGE,"E3"),sQuery(id+"F3.wireOp",EDGE,"E5"),sQuery(id+"F3.wireOp",EDGE,"E8.MirrorCS")])]}),"instanceName":"59"});
            var Q60;
            Q60=makeQuery(id+"F9.opPattern","COPY",BODY,{"derivedFrom":makeQuery(id+"F5.opExtrude","SWEPT_BODY",BODY,{"disambiguationData":[OSD([sQuery(id+"F3.wireOp",EDGE,"E0"),sQuery(id+"F3.wireOp",EDGE,"E3"),sQuery(id+"F3.wireOp",EDGE,"E5"),sQuery(id+"F3.wireOp",EDGE,"E8.MirrorCS")])]}),"instanceName":"60"});
            var Q61;
            Q61=makeQuery(id+"F9.opPattern","COPY",BODY,{"derivedFrom":makeQuery(id+"F5.opExtrude","SWEPT_BODY",BODY,{"disambiguationData":[OSD([sQuery(id+"F3.wireOp",EDGE,"E0"),sQuery(id+"F3.wireOp",EDGE,"E3"),sQuery(id+"F3.wireOp",EDGE,"E5"),sQuery(id+"F3.wireOp",EDGE,"E8.MirrorCS")])]}),"instanceName":"61"});
            var Q62;
            Q62=makeQuery(id+"F9.opPattern","COPY",BODY,{"derivedFrom":makeQuery(id+"F5.opExtrude","SWEPT_BODY",BODY,{"disambiguationData":[OSD([sQuery(id+"F3.wireOp",EDGE,"E0"),sQuery(id+"F3.wireOp",EDGE,"E3"),sQuery(id+"F3.wireOp",EDGE,"E5"),sQuery(id+"F3.wireOp",EDGE,"E8.MirrorCS")])]}),"instanceName":"62"});
            var Q63;
            Q63=makeQuery(id+"F9.opPattern","COPY",BODY,{"derivedFrom":makeQuery(id+"F5.opExtrude","SWEPT_BODY",BODY,{"disambiguationData":[OSD([sQuery(id+"F3.wireOp",EDGE,"E0"),sQuery(id+"F3.wireOp",EDGE,"E3"),sQuery(id+"F3.wireOp",EDGE,"E5"),sQuery(id+"F3.wireOp",EDGE,"E8.MirrorCS")])]}),"instanceName":"63"});
            var Q64;
            Q64=makeQuery(id+"F9.opPattern","COPY",BODY,{"derivedFrom":makeQuery(id+"F5.opExtrude","SWEPT_BODY",BODY,{"disambiguationData":[OSD([sQuery(id+"F3.wireOp",EDGE,"E0"),sQuery(id+"F3.wireOp",EDGE,"E3"),sQuery(id+"F3.wireOp",EDGE,"E5"),sQuery(id+"F3.wireOp",EDGE,"E8.MirrorCS")])]}),"instanceName":"64"});
            var Q65;
            Q65=makeQuery(id+"F9.opPattern","COPY",BODY,{"derivedFrom":makeQuery(id+"F5.opExtrude","SWEPT_BODY",BODY,{"disambiguationData":[OSD([sQuery(id+"F3.wireOp",EDGE,"E0"),sQuery(id+"F3.wireOp",EDGE,"E3"),sQuery(id+"F3.wireOp",EDGE,"E5"),sQuery(id+"F3.wireOp",EDGE,"E8.MirrorCS")])]}),"instanceName":"65"});
            var Q66;
            Q66=makeQuery(id+"F9.opPattern","COPY",BODY,{"derivedFrom":makeQuery(id+"F5.opExtrude","SWEPT_BODY",BODY,{"disambiguationData":[OSD([sQuery(id+"F3.wireOp",EDGE,"E0"),sQuery(id+"F3.wireOp",EDGE,"E3"),sQuery(id+"F3.wireOp",EDGE,"E5"),sQuery(id+"F3.wireOp",EDGE,"E8.MirrorCS")])]}),"instanceName":"66"});
            var Q67;
            Q67=makeQuery(id+"F9.opPattern","COPY",BODY,{"derivedFrom":makeQuery(id+"F5.opExtrude","SWEPT_BODY",BODY,{"disambiguationData":[OSD([sQuery(id+"F3.wireOp",EDGE,"E0"),sQuery(id+"F3.wireOp",EDGE,"E3"),sQuery(id+"F3.wireOp",EDGE,"E5"),sQuery(id+"F3.wireOp",EDGE,"E8.MirrorCS")])]}),"instanceName":"67"});
            var Q68;
            Q68=makeQuery(id+"F9.opPattern","COPY",BODY,{"derivedFrom":makeQuery(id+"F5.opExtrude","SWEPT_BODY",BODY,{"disambiguationData":[OSD([sQuery(id+"F3.wireOp",EDGE,"E0"),sQuery(id+"F3.wireOp",EDGE,"E3"),sQuery(id+"F3.wireOp",EDGE,"E5"),sQuery(id+"F3.wireOp",EDGE,"E8.MirrorCS")])]}),"instanceName":"68"});
            var Q69;
            Q69=makeQuery(id+"F9.opPattern","COPY",BODY,{"derivedFrom":makeQuery(id+"F5.opExtrude","SWEPT_BODY",BODY,{"disambiguationData":[OSD([sQuery(id+"F3.wireOp",EDGE,"E0"),sQuery(id+"F3.wireOp",EDGE,"E3"),sQuery(id+"F3.wireOp",EDGE,"E5"),sQuery(id+"F3.wireOp",EDGE,"E8.MirrorCS")])]}),"instanceName":"69"});
            var Q70;
            Q70=makeQuery(id+"F9.opPattern","COPY",BODY,{"derivedFrom":makeQuery(id+"F5.opExtrude","SWEPT_BODY",BODY,{"disambiguationData":[OSD([sQuery(id+"F3.wireOp",EDGE,"E0"),sQuery(id+"F3.wireOp",EDGE,"E3"),sQuery(id+"F3.wireOp",EDGE,"E5"),sQuery(id+"F3.wireOp",EDGE,"E8.MirrorCS")])]}),"instanceName":"70"});
            var Q71;
            Q71=makeQuery(id+"F9.opPattern","COPY",BODY,{"derivedFrom":makeQuery(id+"F5.opExtrude","SWEPT_BODY",BODY,{"disambiguationData":[OSD([sQuery(id+"F3.wireOp",EDGE,"E0"),sQuery(id+"F3.wireOp",EDGE,"E3"),sQuery(id+"F3.wireOp",EDGE,"E5"),sQuery(id+"F3.wireOp",EDGE,"E8.MirrorCS")])]}),"instanceName":"71"});
            var Q72;
            Q72=makeQuery(id+"F9.opPattern","COPY",BODY,{"derivedFrom":makeQuery(id+"F5.opExtrude","SWEPT_BODY",BODY,{"disambiguationData":[OSD([sQuery(id+"F3.wireOp",EDGE,"E0"),sQuery(id+"F3.wireOp",EDGE,"E3"),sQuery(id+"F3.wireOp",EDGE,"E5"),sQuery(id+"F3.wireOp",EDGE,"E8.MirrorCS")])]}),"instanceName":"72"});
            var Q73;
            Q73=makeQuery(id+"F9.opPattern","COPY",BODY,{"derivedFrom":makeQuery(id+"F5.opExtrude","SWEPT_BODY",BODY,{"disambiguationData":[OSD([sQuery(id+"F3.wireOp",EDGE,"E0"),sQuery(id+"F3.wireOp",EDGE,"E3"),sQuery(id+"F3.wireOp",EDGE,"E5"),sQuery(id+"F3.wireOp",EDGE,"E8.MirrorCS")])]}),"instanceName":"73"});
            var Q74;
            Q74=makeQuery(id+"F9.opPattern","COPY",BODY,{"derivedFrom":makeQuery(id+"F5.opExtrude","SWEPT_BODY",BODY,{"disambiguationData":[OSD([sQuery(id+"F3.wireOp",EDGE,"E0"),sQuery(id+"F3.wireOp",EDGE,"E3"),sQuery(id+"F3.wireOp",EDGE,"E5"),sQuery(id+"F3.wireOp",EDGE,"E8.MirrorCS")])]}),"instanceName":"74"});
            var Q75;
            Q75=makeQuery(id+"F9.opPattern","COPY",BODY,{"derivedFrom":makeQuery(id+"F5.opExtrude","SWEPT_BODY",BODY,{"disambiguationData":[OSD([sQuery(id+"F3.wireOp",EDGE,"E0"),sQuery(id+"F3.wireOp",EDGE,"E3"),sQuery(id+"F3.wireOp",EDGE,"E5"),sQuery(id+"F3.wireOp",EDGE,"E8.MirrorCS")])]}),"instanceName":"75"});
            var Q76;
            Q76=makeQuery(id+"F9.opPattern","COPY",BODY,{"derivedFrom":makeQuery(id+"F5.opExtrude","SWEPT_BODY",BODY,{"disambiguationData":[OSD([sQuery(id+"F3.wireOp",EDGE,"E0"),sQuery(id+"F3.wireOp",EDGE,"E3"),sQuery(id+"F3.wireOp",EDGE,"E5"),sQuery(id+"F3.wireOp",EDGE,"E8.MirrorCS")])]}),"instanceName":"76"});
            var Q77;
            Q77=makeQuery(id+"F9.opPattern","COPY",BODY,{"derivedFrom":makeQuery(id+"F5.opExtrude","SWEPT_BODY",BODY,{"disambiguationData":[OSD([sQuery(id+"F3.wireOp",EDGE,"E0"),sQuery(id+"F3.wireOp",EDGE,"E3"),sQuery(id+"F3.wireOp",EDGE,"E5"),sQuery(id+"F3.wireOp",EDGE,"E8.MirrorCS")])]}),"instanceName":"77"});
            var Q78;
            Q78=makeQuery(id+"F9.opPattern","COPY",BODY,{"derivedFrom":makeQuery(id+"F5.opExtrude","SWEPT_BODY",BODY,{"disambiguationData":[OSD([sQuery(id+"F3.wireOp",EDGE,"E0"),sQuery(id+"F3.wireOp",EDGE,"E3"),sQuery(id+"F3.wireOp",EDGE,"E5"),sQuery(id+"F3.wireOp",EDGE,"E8.MirrorCS")])]}),"instanceName":"78"});
            var Q79;
            Q79=makeQuery(id+"F9.opPattern","COPY",BODY,{"derivedFrom":makeQuery(id+"F5.opExtrude","SWEPT_BODY",BODY,{"disambiguationData":[OSD([sQuery(id+"F3.wireOp",EDGE,"E0"),sQuery(id+"F3.wireOp",EDGE,"E3"),sQuery(id+"F3.wireOp",EDGE,"E5"),sQuery(id+"F3.wireOp",EDGE,"E8.MirrorCS")])]}),"instanceName":"79"});
            var Q80;
            Q80=makeQuery(id+"F9.opPattern","COPY",BODY,{"derivedFrom":makeQuery(id+"F5.opExtrude","SWEPT_BODY",BODY,{"disambiguationData":[OSD([sQuery(id+"F3.wireOp",EDGE,"E0"),sQuery(id+"F3.wireOp",EDGE,"E3"),sQuery(id+"F3.wireOp",EDGE,"E5"),sQuery(id+"F3.wireOp",EDGE,"E8.MirrorCS")])]}),"instanceName":"80"});
            var Q81;
            Q81=makeQuery(id+"F9.opPattern","COPY",BODY,{"derivedFrom":makeQuery(id+"F5.opExtrude","SWEPT_BODY",BODY,{"disambiguationData":[OSD([sQuery(id+"F3.wireOp",EDGE,"E0"),sQuery(id+"F3.wireOp",EDGE,"E3"),sQuery(id+"F3.wireOp",EDGE,"E5"),sQuery(id+"F3.wireOp",EDGE,"E8.MirrorCS")])]}),"instanceName":"81"});
            var Q82;
            Q82=makeQuery(id+"F9.opPattern","COPY",BODY,{"derivedFrom":makeQuery(id+"F5.opExtrude","SWEPT_BODY",BODY,{"disambiguationData":[OSD([sQuery(id+"F3.wireOp",EDGE,"E0"),sQuery(id+"F3.wireOp",EDGE,"E3"),sQuery(id+"F3.wireOp",EDGE,"E5"),sQuery(id+"F3.wireOp",EDGE,"E8.MirrorCS")])]}),"instanceName":"82"});
            var Q83;
            Q83=makeQuery(id+"F9.opPattern","COPY",BODY,{"derivedFrom":makeQuery(id+"F5.opExtrude","SWEPT_BODY",BODY,{"disambiguationData":[OSD([sQuery(id+"F3.wireOp",EDGE,"E0"),sQuery(id+"F3.wireOp",EDGE,"E3"),sQuery(id+"F3.wireOp",EDGE,"E5"),sQuery(id+"F3.wireOp",EDGE,"E8.MirrorCS")])]}),"instanceName":"83"});
            var Q84;
            Q84=makeQuery(id+"F9.opPattern","COPY",BODY,{"derivedFrom":makeQuery(id+"F5.opExtrude","SWEPT_BODY",BODY,{"disambiguationData":[OSD([sQuery(id+"F3.wireOp",EDGE,"E0"),sQuery(id+"F3.wireOp",EDGE,"E3"),sQuery(id+"F3.wireOp",EDGE,"E5"),sQuery(id+"F3.wireOp",EDGE,"E8.MirrorCS")])]}),"instanceName":"84"});
            var Q85;
            Q85=makeQuery(id+"F9.opPattern","COPY",BODY,{"derivedFrom":makeQuery(id+"F5.opExtrude","SWEPT_BODY",BODY,{"disambiguationData":[OSD([sQuery(id+"F3.wireOp",EDGE,"E0"),sQuery(id+"F3.wireOp",EDGE,"E3"),sQuery(id+"F3.wireOp",EDGE,"E5"),sQuery(id+"F3.wireOp",EDGE,"E8.MirrorCS")])]}),"instanceName":"85"});
            var Q86;
            Q86=makeQuery(id+"F9.opPattern","COPY",BODY,{"derivedFrom":makeQuery(id+"F5.opExtrude","SWEPT_BODY",BODY,{"disambiguationData":[OSD([sQuery(id+"F3.wireOp",EDGE,"E0"),sQuery(id+"F3.wireOp",EDGE,"E3"),sQuery(id+"F3.wireOp",EDGE,"E5"),sQuery(id+"F3.wireOp",EDGE,"E8.MirrorCS")])]}),"instanceName":"86"});
            var Q87;
            Q87=makeQuery(id+"F9.opPattern","COPY",BODY,{"derivedFrom":makeQuery(id+"F5.opExtrude","SWEPT_BODY",BODY,{"disambiguationData":[OSD([sQuery(id+"F3.wireOp",EDGE,"E0"),sQuery(id+"F3.wireOp",EDGE,"E3"),sQuery(id+"F3.wireOp",EDGE,"E5"),sQuery(id+"F3.wireOp",EDGE,"E8.MirrorCS")])]}),"instanceName":"87"});
            var Q88;
            Q88=makeQuery(id+"F9.opPattern","COPY",BODY,{"derivedFrom":makeQuery(id+"F5.opExtrude","SWEPT_BODY",BODY,{"disambiguationData":[OSD([sQuery(id+"F3.wireOp",EDGE,"E0"),sQuery(id+"F3.wireOp",EDGE,"E3"),sQuery(id+"F3.wireOp",EDGE,"E5"),sQuery(id+"F3.wireOp",EDGE,"E8.MirrorCS")])]}),"instanceName":"88"});
            var Q89;
            Q89=makeQuery(id+"F9.opPattern","COPY",BODY,{"derivedFrom":makeQuery(id+"F5.opExtrude","SWEPT_BODY",BODY,{"disambiguationData":[OSD([sQuery(id+"F3.wireOp",EDGE,"E0"),sQuery(id+"F3.wireOp",EDGE,"E3"),sQuery(id+"F3.wireOp",EDGE,"E5"),sQuery(id+"F3.wireOp",EDGE,"E8.MirrorCS")])]}),"instanceName":"89"});
            var Q90;
            Q90=makeQuery(id+"F8.opExtrude","SWEPT_BODY",BODY,{"disambiguationData":[OSD([sQuery(id+"F4.wireOp",EDGE,"E10")])]});
            booleanBodies(context, id + "F10", {"operationType" : BooleanOperationType.SUBTRACTION, "tools" : qUnion([Q0, Q1, Q2, Q3, Q4, Q5, Q6, Q7, Q8, Q9, Q10, Q11, Q12, Q13, Q14, Q15, Q16, Q17, Q18, Q19, Q20, Q21, Q22, Q23, Q24, Q25, Q26, Q27, Q28, Q29, Q30, Q31, Q32, Q33, Q34, Q35, Q36, Q37, Q38, Q39, Q40, Q41, Q42, Q43, Q44, Q45, Q46, Q47, Q48, Q49, Q50, Q51, Q52, Q53, Q54, Q55, Q56, Q57, Q58, Q59, Q60, Q61, Q62, Q63, Q64, Q65, Q66, Q67, Q68, Q69, Q70, Q71, Q72, Q73, Q74, Q75, Q76, Q77, Q78, Q79, Q80, Q81, Q82, Q83, Q84, Q85, Q86, Q87, Q88, Q89]), "targets" : qUnion([Q90])});
        }
        {
            var Q0;
            Q0=makeQuery(id+"F8.opExtrude","CAP_FACE",FACE,{"disambiguationData":[OSD([sQuery(id+"F4.wireOp",EDGE,"E10")])],"isStart":true});
            var sketch = newSketch(context, id + "F11", { "sketchPlane" : qUnion([Q0])});
            skCircle(sketch, "E12", {"center": v(0, 0) * mm, "radius": 5.16 * mm});
            skCircle(sketch, "E13", {"center": v(0, 0) * mm, "radius": 10.16 * mm});
            skCircle(sketch, "E14", {"center": v(0, 0) * mm, "radius": 17.43 * mm});
            skLineSegment(sketch, "E15", {"start": v(0, 0) * mm, "end": v(0, 17.43) * mm, "construction": true});
            skLineSegment(sketch, "E16.0", {"start": v(2.5, 0) * mm, "end": v(2.5, 17.25) * mm});
            skLineSegment(sketch, "E17", {"start": v(0, 0) * mm, "end": v(19.43, -11.22) * mm, "construction": true});
            skLineSegment(sketch, "E18.0", {"start": v(1.25, 2.17) * mm, "end": v(20.55, -8.98) * mm});
            skCircle(sketch, "E19", {"center": v(0, 0) * mm, "radius": 22.43 * mm});
            skSolve(sketch);
        }
        {
            var Q0;
            Q0=makeQuery(id+"F11.imprint","IMPRINT",FACE,{"disambiguationData":[TD([[makeQuery(id+"F11.imprint","IMPRINT",EDGE,{"derivedFrom":sQuery(id+"F11.wireOp",EDGE,"E12")}),1.0]])]});
            extrude(context, id + "F12", {"entities" : qUnion([Q0]), "operationType" : NewBodyOperationType.REMOVE, "oppositeDirection" : true, "depth" : 25 * mm});
        }
        {
            var Q0;
            {var subQ0=sQuery(id+"F11.wireOp",EDGE,"E16.0");var subQ1=sQuery(id+"F11.wireOp",EDGE,"E13");var subQ2=makeQuery(id+"F11.imprint","INTERSECT",VERTEX,{"derivedFrom":[subQ1,subQ0]});Q0=makeQuery(id+"F11.imprint","IMPRINT",FACE,{"disambiguationData":[TD([[makeQuery(id+"F11.imprint","IMPRINT",EDGE,{"disambiguationData":[TD([[subQ2,1.0]])],"derivedFrom":subQ1}),-1.0]])]});}
            extrude(context, id + "F13", {"entities" : qUnion([Q0]), "oppositeDirection" : true, "depth" : 6 * mm, "offsetDistance" : 25 * mm});
        }
        {
            var Q0;
            Q0=makeQuery(id+"F13.opExtrude","SWEPT_EDGE",EDGE,{"disambiguationData":[OSD([sQuery(id+"F11.wireOp",EDGE,"E14"),sQuery(id+"F11.wireOp",EDGE,"E16.0")])]});
            var Q1;
            Q1=makeQuery(id+"F13.opExtrude","SWEPT_EDGE",EDGE,{"disambiguationData":[OSD([sQuery(id+"F11.wireOp",EDGE,"E13"),sQuery(id+"F11.wireOp",EDGE,"E16.0")])]});
            var Q2;
            Q2=makeQuery(id+"F13.opExtrude","SWEPT_EDGE",EDGE,{"disambiguationData":[OSD([sQuery(id+"F11.wireOp",EDGE,"E13"),sQuery(id+"F11.wireOp",EDGE,"E18.0")])]});
            var Q3;
            Q3=makeQuery(id+"F13.opExtrude","SWEPT_EDGE",EDGE,{"disambiguationData":[OSD([sQuery(id+"F11.wireOp",EDGE,"E14"),sQuery(id+"F11.wireOp",EDGE,"E18.0")])]});
            fillet(context, id + "F14", {"entities" : qUnion([Q0, Q1, Q2, Q3]), "radius" : (getVariable(context, 'SF')) * mm, "tangentPropagation" : true, "allowEdgeOverflow" : false});
        }
        {
            var Q0;
            Q0=makeQuery(id+"F13.opExtrude","SWEPT_BODY",BODY,{"disambiguationData":[OSD([sQuery(id+"F11.wireOp",EDGE,"E13"),sQuery(id+"F11.wireOp",EDGE,"E14"),sQuery(id+"F11.wireOp",EDGE,"E16.0"),sQuery(id+"F11.wireOp",EDGE,"E18.0")])]});
            var Q1;
            Q1=makeQuery(id+"F12.boolean.opBoolean","INTERSECT",EDGE,{"derivedFrom":[makeQuery(id+"F8.opExtrude","CAP_FACE",FACE,{"disambiguationData":[OSD([sQuery(id+"F4.wireOp",EDGE,"E10")])],"isStart":false}),makeQuery(id+"F12.opExtrude","SWEPT_FACE",FACE,{"disambiguationData":[OSD([sQuery(id+"F11.wireOp",EDGE,"E12")])]})]});
            circularPattern(context, id + "F15", {"entities" : qUnion([Q0]), "axis" : qUnion([Q1]), "angle" : 360 * degree, "instanceCount" : getVariable(context, 'SP'), "equalSpace" : true});
        }
        {
            var Q0;
            Q0=makeQuery(id+"F15.opPattern","COPY",BODY,{"derivedFrom":makeQuery(id+"F13.opExtrude","SWEPT_BODY",BODY,{"disambiguationData":[OSD([sQuery(id+"F11.wireOp",EDGE,"E13"),sQuery(id+"F11.wireOp",EDGE,"E14"),sQuery(id+"F11.wireOp",EDGE,"E16.0"),sQuery(id+"F11.wireOp",EDGE,"E18.0")])]}),"instanceName":"2"});
            var Q1;
            Q1=makeQuery(id+"F15.opPattern","COPY",BODY,{"derivedFrom":makeQuery(id+"F13.opExtrude","SWEPT_BODY",BODY,{"disambiguationData":[OSD([sQuery(id+"F11.wireOp",EDGE,"E13"),sQuery(id+"F11.wireOp",EDGE,"E14"),sQuery(id+"F11.wireOp",EDGE,"E16.0"),sQuery(id+"F11.wireOp",EDGE,"E18.0")])]}),"instanceName":"1"});
            var Q2;
            Q2=makeQuery(id+"F13.opExtrude","SWEPT_BODY",BODY,{"disambiguationData":[OSD([sQuery(id+"F11.wireOp",EDGE,"E13"),sQuery(id+"F11.wireOp",EDGE,"E14"),sQuery(id+"F11.wireOp",EDGE,"E16.0"),sQuery(id+"F11.wireOp",EDGE,"E18.0")])]});
            var Q3;
            Q3=makeQuery(id+"F15.opPattern","COPY",BODY,{"derivedFrom":makeQuery(id+"F13.opExtrude","SWEPT_BODY",BODY,{"disambiguationData":[OSD([sQuery(id+"F11.wireOp",EDGE,"E13"),sQuery(id+"F11.wireOp",EDGE,"E14"),sQuery(id+"F11.wireOp",EDGE,"E16.0"),sQuery(id+"F11.wireOp",EDGE,"E18.0")])]}),"instanceName":"3"});
            var Q4;
            Q4=makeQuery(id+"F15.opPattern","COPY",BODY,{"derivedFrom":makeQuery(id+"F13.opExtrude","SWEPT_BODY",BODY,{"disambiguationData":[OSD([sQuery(id+"F11.wireOp",EDGE,"E13"),sQuery(id+"F11.wireOp",EDGE,"E14"),sQuery(id+"F11.wireOp",EDGE,"E16.0"),sQuery(id+"F11.wireOp",EDGE,"E18.0")])]}),"instanceName":"4"});
            var Q5;
            Q5=makeQuery(id+"F15.opPattern","COPY",BODY,{"derivedFrom":makeQuery(id+"F13.opExtrude","SWEPT_BODY",BODY,{"disambiguationData":[OSD([sQuery(id+"F11.wireOp",EDGE,"E13"),sQuery(id+"F11.wireOp",EDGE,"E14"),sQuery(id+"F11.wireOp",EDGE,"E16.0"),sQuery(id+"F11.wireOp",EDGE,"E18.0")])]}),"instanceName":"5"});
            var Q6;
            Q6=makeQuery(id+"F8.opExtrude","SWEPT_BODY",BODY,{"disambiguationData":[OSD([sQuery(id+"F4.wireOp",EDGE,"E10")])]});
            booleanBodies(context, id + "F16", {"operationType" : BooleanOperationType.SUBTRACTION, "tools" : qUnion([Q0, Q1, Q2, Q3, Q4, Q5]), "targets" : qUnion([Q6])});
        }
    });
